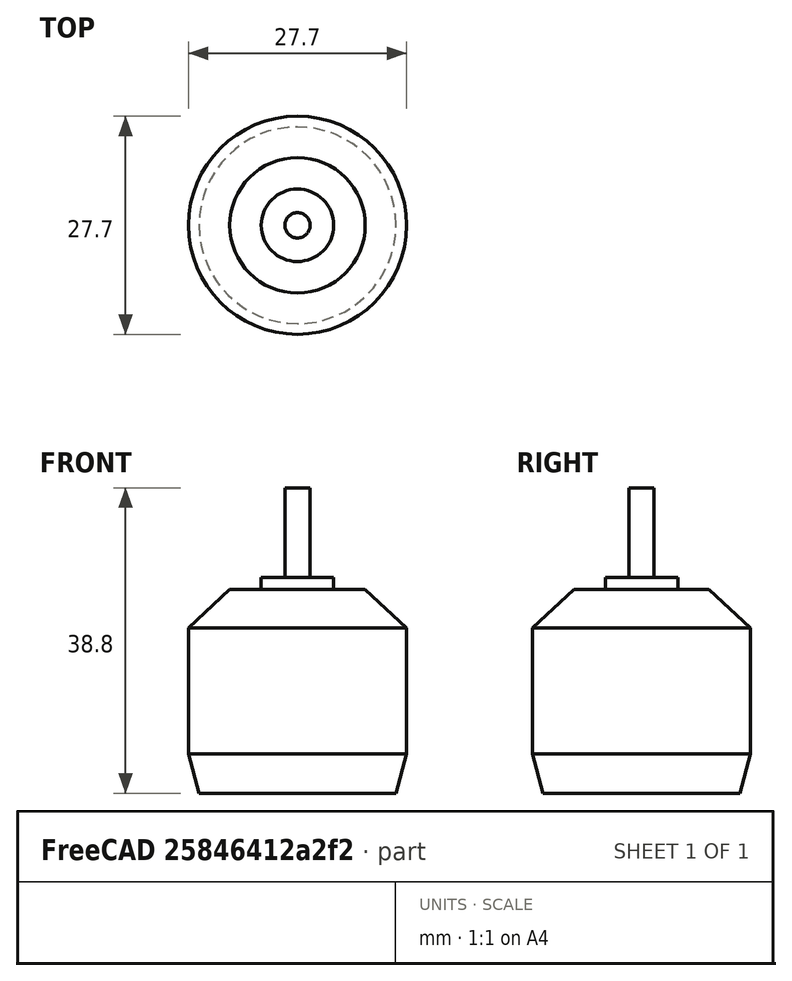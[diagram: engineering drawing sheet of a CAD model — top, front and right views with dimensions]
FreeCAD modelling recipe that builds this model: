
FCSTD DOCUMENT  (FreeCAD 0.17R13543 (Git))
Label: A2213_13T_1000KV
License: All rights reserved
LicenseURL: http://en.wikipedia.org/wiki/All_rights_reserved
objects: Sketcher::SketchObject×1, PartDesign::Revolution×1, PartDesign::Body×1, App::Part×1
note: 4 computed .brp shape members not serialized (recipe doc carries the construction recipe); baked Part::Feature solids carry a one-line shape summary decoded from their .brp

FEATURE [Sketcher::SketchObject] Sketch
  MapMode = 5
  Placement = pos=(0,0,0) rot=(1,0,0;1.5708rad)
  Support = -> [XZ_Plane001]
  sketch-geometry (10):
    g0: LineSegment StartX=0 StartY=0 StartZ=0 EndX=0 EndY=38.8 EndZ=0
    g1: LineSegment StartX=0 StartY=38.8 StartZ=0 EndX=1.6 EndY=38.8 EndZ=0
    g2: LineSegment StartX=1.6 StartY=38.8 StartZ=0 EndX=1.6 EndY=27.4 EndZ=0
    g3: LineSegment StartX=1.6 StartY=27.4 StartZ=0 EndX=4.6 EndY=27.4 EndZ=0
    g4: LineSegment StartX=4.6 StartY=27.4 StartZ=0 EndX=4.6 EndY=25.9 EndZ=0
    g5: LineSegment StartX=4.6 StartY=25.9 StartZ=0 EndX=8.6 EndY=25.9 EndZ=0
    g6: LineSegment StartX=8.6 StartY=25.9 StartZ=0 EndX=13.85 EndY=21 EndZ=0
    g7: LineSegment StartX=13.85 StartY=21 StartZ=0 EndX=13.85 EndY=5 EndZ=0
    g8: LineSegment StartX=13.85 StartY=5 StartZ=0 EndX=12.5 EndY=0 EndZ=0
    g9: LineSegment StartX=12.5 StartY=0 StartZ=0 EndX=0 EndY=0 EndZ=0
  constraints (30):
    c: Coincident(g0,g-1)
    c: PointOnObject(g0,g-2)
    c: Coincident(g1,g0)
    c: Horizontal(g1)
    c: Coincident(g2,g1)
    c: Vertical(g2)
    c: Coincident(g3,g2)
    c: Horizontal(g3)
    c: Coincident(g4,g3)
    c: Vertical(g4)
    c: Coincident(g5,g4)
    c: Horizontal(g5)
    c: Coincident(g6,g5)
    c: Coincident(g7,g6)
    c: Vertical(g7)
    c: Coincident(g8,g7)
    c: PointOnObject(g8,g-1)
    c: Coincident(g9,g8)
    c: Horizontal(g9)
    c: DistanceX(g-1,g7) = 13.85
    c: DistanceX(g-1,g8) = 12.5
    c: DistanceY(g8,g7) = 5
    c: DistanceY(g-1,g0) = 38.8
    c: DistanceY(g2,g1) = 11.4
    c: DistanceY(g4,g3) = 1.5
    c: DistanceX(g4,g5) = 4
    c: DistanceY(g7,g6) = 16
    c: DistanceX(g0,g1) = 1.6
    c: DistanceX(g2,g3) = 3
    c: Coincident(g9,g-1)
FEATURE [PartDesign::Revolution] Revolution
  Angle = 360
  Axis = (0,0,1)
  Base = (0,0,0)
  Placement = pos=(0,0,0) rot=(1,0,0;1.5708rad)
  Profile = -> Sketch
  ReferenceAxis = -> Sketch [V_Axis]
  Reversed = true
FEATURE [PartDesign::Body] Body
  Group = -> [Sketch,Revolution]
  Origin = -> Origin001
  Tip = -> Revolution
FEATURE [App::Part] Part
  Group = -> [Body]
  License = CC BY 3.0
  LicenseURL = http://creativecommons.org/licenses/by/3.0/
  Origin = -> Origin
